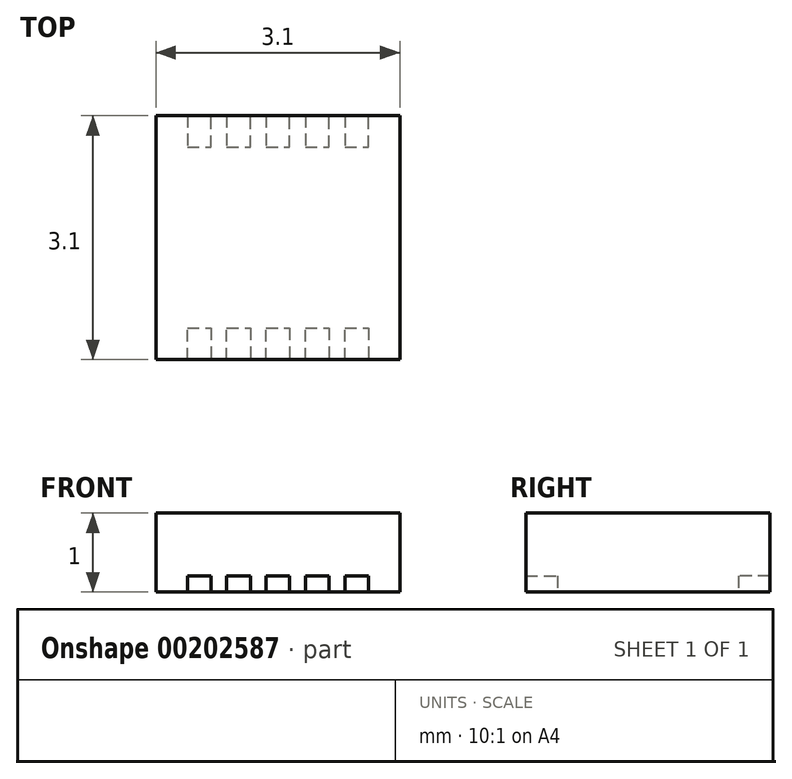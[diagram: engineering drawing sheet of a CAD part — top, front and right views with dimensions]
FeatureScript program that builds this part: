
annotation { "Feature Type Name" : "Feature", "Feature Type Description" : "" }
export const myFeature = defineFeature(function(context is Context, id is Id, definition is map)
    precondition{}
    {
        {
            var Q0;
            Q0=qCreatedBy(makeId("Top.planeOp"),FACE);
            var sketch = newSketch(context, id + "F0", { "sketchPlane" : qUnion([Q0])});
            skLineSegment(sketch, "E0.bottom", {"start": v(1.55, 1.55) * mm, "end": v(-1.55, 1.55) * mm});
            skLineSegment(sketch, "E0.top", {"start": v(1.55, -1.55) * mm, "end": v(-1.55, -1.55) * mm});
            skLineSegment(sketch, "E0.left", {"start": v(1.55, 1.55) * mm, "end": v(1.55, -1.55) * mm});
            skLineSegment(sketch, "E0.right", {"start": v(-1.55, 1.55) * mm, "end": v(-1.55, -1.55) * mm});
            skPoint(sketch, "E0.middle", {"position": v(0, 0) * mm});
            skSolve(sketch);
        }
        {
            var Q0;
            Q0=makeQuery(id+"F0.imprint","IMPRINT",FACE,{"disambiguationData":[TD([[makeQuery(id+"F0.imprint","IMPRINT",EDGE,{"derivedFrom":sQuery(id+"F0.wireOp",EDGE,"E0.bottom")}),1.0]])]});
            extrude(context, id + "F1", {"entities" : qUnion([Q0]), "depth" : 1 * mm});
        }
        {
            var Q0;
            Q0=makeQuery(id+"F1.opExtrude","CAP_FACE",FACE,{"disambiguationData":[OSD([sQuery(id+"F0.wireOp",EDGE,"E0.bottom"),sQuery(id+"F0.wireOp",EDGE,"E0.top"),sQuery(id+"F0.wireOp",EDGE,"E0.left"),sQuery(id+"F0.wireOp",EDGE,"E0.right")])],"isStart":true});
            var sketch = newSketch(context, id + "F2", { "sketchPlane" : qUnion([Q0])});
            skLineSegment(sketch, "E1", {"start": v(0, -1.55) * mm, "end": v(0, 1.55) * mm, "construction": true});
            skLineSegment(sketch, "E2", {"start": v(-0.15, 1.55) * mm, "end": v(-0.15, 1.15) * mm});
            skLineSegment(sketch, "E3", {"start": v(-0.15, 1.15) * mm, "end": v(0.15, 1.15) * mm});
            skLineSegment(sketch, "E4", {"start": v(0.15, 1.15) * mm, "end": v(0.15, 1.55) * mm});
            skLineSegment(sketch, "E5", {"start": v(0.15, 1.55) * mm, "end": v(-0.15, 1.55) * mm});
            skLineSegment(sketch, "E6.1.0.0", {"start": v(0.35, 1.15) * mm, "end": v(0.65, 1.15) * mm});
            skLineSegment(sketch, "E6.1.0.1", {"start": v(0.65, 1.15) * mm, "end": v(0.65, 1.55) * mm});
            skLineSegment(sketch, "E6.1.0.2", {"start": v(0.35, 1.55) * mm, "end": v(0.35, 1.15) * mm});
            skLineSegment(sketch, "E6.1.0.3", {"start": v(0.65, 1.55) * mm, "end": v(0.35, 1.55) * mm});
            skLineSegment(sketch, "E6.2.0.0", {"start": v(0.85, 1.15) * mm, "end": v(1.15, 1.15) * mm});
            skLineSegment(sketch, "E6.2.0.1", {"start": v(1.15, 1.15) * mm, "end": v(1.15, 1.55) * mm});
            skLineSegment(sketch, "E6.2.0.2", {"start": v(0.85, 1.55) * mm, "end": v(0.85, 1.15) * mm});
            skLineSegment(sketch, "E6.2.0.3", {"start": v(1.15, 1.55) * mm, "end": v(0.85, 1.55) * mm});
            skLineSegment(sketch, "E7.1.0.0", {"start": v(-0.35, 1.15) * mm, "end": v(-0.35, 1.55) * mm});
            skLineSegment(sketch, "E7.1.0.1", {"start": v(-0.35, 1.55) * mm, "end": v(-0.65, 1.55) * mm});
            skLineSegment(sketch, "E7.1.0.2", {"start": v(-0.65, 1.15) * mm, "end": v(-0.35, 1.15) * mm});
            skLineSegment(sketch, "E7.1.0.3", {"start": v(-0.65, 1.55) * mm, "end": v(-0.65, 1.15) * mm});
            skLineSegment(sketch, "E7.2.0.0", {"start": v(-0.85, 1.15) * mm, "end": v(-0.85, 1.55) * mm});
            skLineSegment(sketch, "E7.2.0.1", {"start": v(-0.85, 1.55) * mm, "end": v(-1.15, 1.55) * mm});
            skLineSegment(sketch, "E7.2.0.2", {"start": v(-1.15, 1.15) * mm, "end": v(-0.85, 1.15) * mm});
            skLineSegment(sketch, "E7.2.0.3", {"start": v(-1.15, 1.55) * mm, "end": v(-1.15, 1.15) * mm});
            skLineSegment(sketch, "E8.MirrorCS", {"start": v(-0.15, -1.15) * mm, "end": v(0.15, -1.15) * mm});
            skLineSegment(sketch, "E9.MirrorCS", {"start": v(-0.15, -1.55) * mm, "end": v(-0.15, -1.15) * mm});
            skLineSegment(sketch, "E10.MirrorCS", {"start": v(0.65, -1.55) * mm, "end": v(0.35, -1.55) * mm});
            skLineSegment(sketch, "E11.MirrorCS", {"start": v(-0.35, -1.55) * mm, "end": v(-0.65, -1.55) * mm});
            skLineSegment(sketch, "E12.MirrorCS", {"start": v(0, 1.55) * mm, "end": v(0, -1.55) * mm, "construction": true});
            skLineSegment(sketch, "E13.MirrorCS", {"start": v(-0.65, -1.15) * mm, "end": v(-0.35, -1.15) * mm});
            skLineSegment(sketch, "E14.MirrorCS", {"start": v(1.15, -1.15) * mm, "end": v(1.15, -1.55) * mm});
            skLineSegment(sketch, "E15.MirrorCS", {"start": v(0.15, -1.15) * mm, "end": v(0.15, -1.55) * mm});
            skLineSegment(sketch, "E16.MirrorCS", {"start": v(0.85, -1.55) * mm, "end": v(0.85, -1.15) * mm});
            skLineSegment(sketch, "E17.MirrorCS", {"start": v(1.15, -1.55) * mm, "end": v(0.85, -1.55) * mm});
            skLineSegment(sketch, "E18.MirrorCS", {"start": v(-0.65, -1.55) * mm, "end": v(-0.65, -1.15) * mm});
            skLineSegment(sketch, "E19.MirrorCS", {"start": v(-1.15, -1.55) * mm, "end": v(-1.15, -1.15) * mm});
            skLineSegment(sketch, "E20.MirrorCS", {"start": v(0.15, -1.55) * mm, "end": v(-0.15, -1.55) * mm});
            skLineSegment(sketch, "E21.MirrorCS", {"start": v(-0.35, -1.15) * mm, "end": v(-0.35, -1.55) * mm});
            skLineSegment(sketch, "E22.MirrorCS", {"start": v(0.35, -1.15) * mm, "end": v(0.65, -1.15) * mm});
            skLineSegment(sketch, "E23.MirrorCS", {"start": v(-0.85, -1.15) * mm, "end": v(-0.85, -1.55) * mm});
            skLineSegment(sketch, "E24.MirrorCS", {"start": v(-0.85, -1.55) * mm, "end": v(-1.15, -1.55) * mm});
            skLineSegment(sketch, "E25.MirrorCS", {"start": v(0.35, -1.55) * mm, "end": v(0.35, -1.15) * mm});
            skLineSegment(sketch, "E26.MirrorCS", {"start": v(0.85, -1.15) * mm, "end": v(1.15, -1.15) * mm});
            skLineSegment(sketch, "E27.MirrorCS", {"start": v(-1.15, -1.15) * mm, "end": v(-0.85, -1.15) * mm});
            skLineSegment(sketch, "E28.MirrorCS", {"start": v(0.65, -1.15) * mm, "end": v(0.65, -1.55) * mm});
            skSolve(sketch);
        }
        {
            var Q0;
            Q0 = qSketchRegion(id + "F2", true);
            extrude(context, id + "F3", {"entities" : qUnion([Q0]), "operationType" : NewBodyOperationType.REMOVE, "oppositeDirection" : true, "depth" : 0.2 * mm});
        }
        {
            var Q0;
            Q0 = qSketchRegion(id + "F2", true);
            extrude(context, id + "F4", {"entities" : qUnion([Q0]), "oppositeDirection" : true, "depth" : 0.2 * mm});
        }
    });
